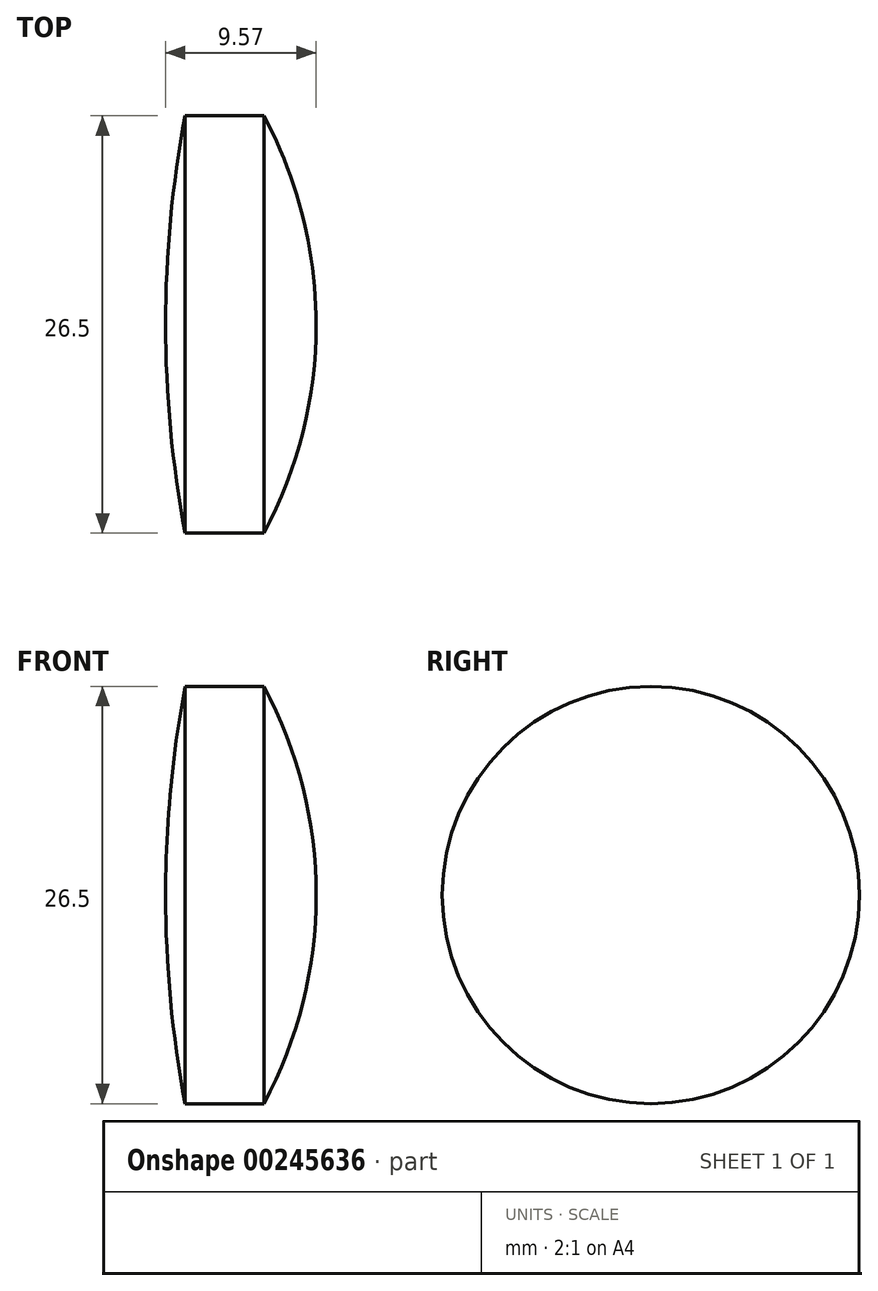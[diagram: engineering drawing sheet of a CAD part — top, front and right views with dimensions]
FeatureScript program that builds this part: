
annotation { "Feature Type Name" : "Feature", "Feature Type Description" : "" }
export const myFeature = defineFeature(function(context is Context, id is Id, definition is map)
    precondition{}
    {
        {
            var Q0;
            Q0=qCreatedBy(makeId("Right.planeOp"),FACE);
            var sketch = newSketch(context, id + "F0", { "sketchPlane" : qUnion([Q0])});
            skCircle(sketch, "E0", {"center": v(0, 0) * mm, "radius": 13.25 * mm});
            skSolve(sketch);
        }
        {
            var Q0;
            Q0 = qSketchRegion(id + "F0", true);
            extrude(context, id + "F1", {"entities" : qUnion([Q0]), "depth" : 5 * mm});
        }
        {
            var Q0;
            Q0=qCreatedBy(makeId("Top.planeOp"),FACE);
            var sketch = newSketch(context, id + "F2", { "sketchPlane" : qUnion([Q0])});
            skLineSegment(sketch, "E1", {"start": v(0, 0) * mm, "end": v(0, -13.25) * mm});
            skLineSegment(sketch, "E2", {"start": v(0, -13.25) * mm, "end": v(0, 13.25) * mm});
            skArc(sketch, "E3", {"start": v(0, 13.25) * mm, "mid": v(-1.63, 0) * mm, "end": v(0, -13.25) * mm});
            skLineSegment(sketch, "E4", {"start": v(0, 13.25) * mm, "end": v(5, 13.25) * mm});
            skLineSegment(sketch, "E5", {"start": v(5, 13.25) * mm, "end": v(5, -13.25) * mm});
            skLineSegment(sketch, "E6", {"start": v(5, -13.25) * mm, "end": v(5, 0) * mm});
            skArc(sketch, "E7", {"start": v(8.33, 0) * mm, "mid": v(7.48, 6.83) * mm, "end": v(5, 13.25) * mm});
            skLineSegment(sketch, "E8", {"start": v(5, 0) * mm, "end": v(8.33, 0) * mm});
            skSolve(sketch);
        }
        {
            var Q0;
            Q0=qCreatedBy(makeId("Top.planeOp"),FACE);
            var sketch = newSketch(context, id + "F3", { "sketchPlane" : qUnion([Q0])});
            skLineSegment(sketch, "E9", {"start": v(0, 0) * mm, "end": v(10.6, 0) * mm});
            skSolve(sketch);
        }
        {
            var Q0;
            Q0=makeQuery(id+"F2.imprint","IMPRINT",FACE,{"disambiguationData":[TD([[makeQuery(id+"F2.imprint","IMPRINT",EDGE,{"derivedFrom":sQuery(id+"F2.wireOp",EDGE,"E5")}),1.0]])]});
            var Q1;
            Q1=sQuery(id+"F3.wireOp",EDGE,"E9");
            revolve(context, id + "F4", {"operationType" : NewBodyOperationType.ADD, "entities" : qUnion([Q0]), "axis" : qUnion([Q1]), "revolveType" : RevolveType.FULL});
        }
        {
            var Q0;
            Q0=qCreatedBy(makeId("Front.planeOp"),FACE);
            var sketch = newSketch(context, id + "F5", { "sketchPlane" : qUnion([Q0])});
            skLineSegment(sketch, "E10", {"start": v(0, 0) * mm, "end": v(0, 13.25) * mm});
            skLineSegment(sketch, "E11", {"start": v(0, 0) * mm, "end": v(0, -13.25) * mm});
            skArc(sketch, "E12", {"start": v(0, 13.25) * mm, "mid": v(-0.93, 6.65) * mm, "end": v(-1.24, 0) * mm});
            skLineSegment(sketch, "E13", {"start": v(0, 0) * mm, "end": v(-1.24, 0) * mm});
            skSolve(sketch);
        }
        {
            var Q0;
            Q0=makeQuery(id+"F5.imprint","IMPRINT",FACE,{"disambiguationData":[TD([[makeQuery(id+"F5.imprint","IMPRINT",EDGE,{"derivedFrom":sQuery(id+"F5.wireOp",EDGE,"E10")}),1.0]])]});
            var Q1;
            Q1=sQuery(id+"F5.wireOp",EDGE,"E13");
            revolve(context, id + "F6", {"operationType" : NewBodyOperationType.ADD, "entities" : qUnion([Q0]), "axis" : qUnion([Q1]), "revolveType" : RevolveType.FULL});
        }
    });
